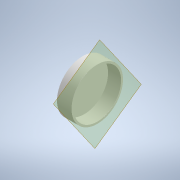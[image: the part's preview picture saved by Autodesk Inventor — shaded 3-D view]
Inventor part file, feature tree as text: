
AUTODESK INVENTOR PART (.ipt)
format: ipt  version: 2020 (Build 240168000, 168)  size: 121,856 bytes
history: native  units: mm
features: other x3, extrude x2, sketch x2, plane x1, reference x1, projected_geometry x1
ambient origin geometry x8: Origin, YZ Plane, XZ Plane, XY Plane, X Axis, Y Axis, Z Axis, Center Point
bodies: Solid1 (feature_tree)
feature tree (10):
  plane  "Work Plane1"
  extrude  "Extrusion1"  Depth=1.0mm TaperAngle=0.0deg
  extrude  "Extrusion2"  [1 undecoded]
  sketch  "Sketch1"  dims[d0=9.327mm d1=0.0mm d2=1.0mm d3=0.0mm]
  reference  "Reference1"
  sketch  "Sketch2"
  projected_geometry  "Projected Loop1"
  other  "<userpath>\Documents\Inventor\CC_RENEV\belzebub.iam"
  other  "belzebub.iam"
  other  "Part5:1"
note: 1 required parameter value undecoded (feature->parameter linkage not recoverable at this tier; creation-order binding heuristic only, values carry confidence <= 0.55)
